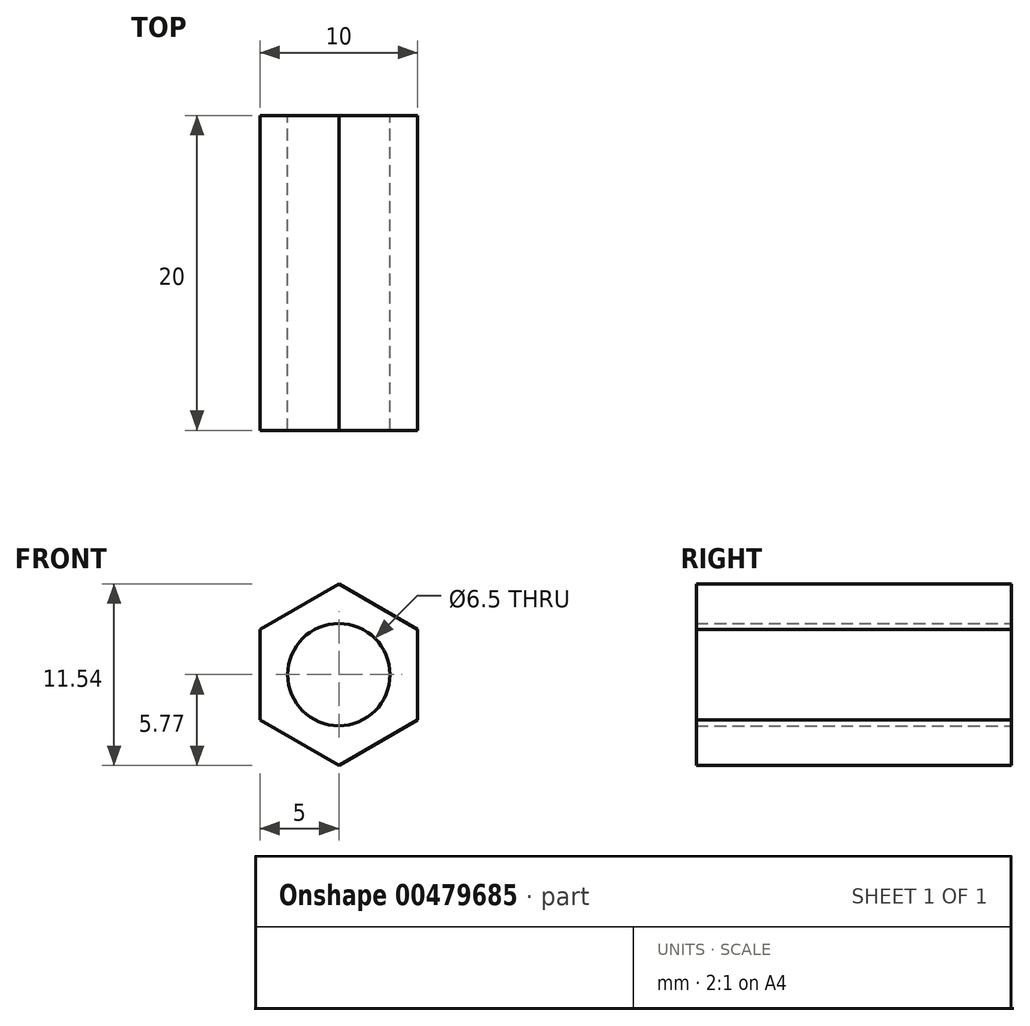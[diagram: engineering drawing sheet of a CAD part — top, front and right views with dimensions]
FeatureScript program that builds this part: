
annotation { "Feature Type Name" : "Feature", "Feature Type Description" : "" }
export const myFeature = defineFeature(function(context is Context, id is Id, definition is map)
    precondition{}
    {
        {
            var Q0;
            Q0=qCreatedBy(makeId("Front.planeOp"),FACE);
            var sketch = newSketch(context, id + "F0", { "sketchPlane" : qUnion([Q0])});
            skLineSegment(sketch, "E0.bottom", {"start": v(5, -5) * mm, "end": v(1.34, -5) * mm});
            skLineSegment(sketch, "E0.left", {"start": v(5, -2.89) * mm, "end": v(5, 2.89) * mm});
            skLineSegment(sketch, "E0.right", {"start": v(-5, -5) * mm, "end": v(-5, 5) * mm});
            skCircle(sketch, "E1", {"center": v(0, 0) * mm, "radius": 5 * mm});
            skPoint(sketch, "E2.start.orphan", {"position": v(5, 0) * mm});
            skPoint(sketch, "E3.orphan", {"position": v(-5, 0) * mm});
            skLineSegment(sketch, "E4", {"start": v(1.34, 5) * mm, "end": v(5, 5) * mm});
            skLineSegment(sketch, "E5", {"start": v(-5, 2.89) * mm, "end": v(-8.07, 4.66) * mm});
            skLineSegment(sketch, "E6", {"start": v(-5, -2.89) * mm, "end": v(-7.12, -4.11) * mm});
            skLineSegment(sketch, "E7", {"start": v(-7.12, -4.11) * mm, "end": v(-5, -2.89) * mm});
            skLineSegment(sketch, "E8", {"start": v(0, -8.43) * mm, "end": v(0, -5.77) * mm});
            skLineSegment(sketch, "E9", {"start": v(5, -2.89) * mm, "end": v(7.12, -4.11) * mm});
            skLineSegment(sketch, "E10", {"start": v(5, 2.89) * mm, "end": v(9.86, 5.7) * mm});
            skLineSegment(sketch, "E11", {"start": v(5, 2.89) * mm, "end": v(0, 5.77) * mm});
            skLineSegment(sketch, "E12", {"start": v(0, 5.77) * mm, "end": v(-5, 2.89) * mm});
            skLineSegment(sketch, "E13", {"start": v(-5, -2.89) * mm, "end": v(0, -5.77) * mm});
            skLineSegment(sketch, "E14", {"start": v(0, -5.77) * mm, "end": v(5, -2.89) * mm});
            skCircle(sketch, "E15", {"center": v(0, 0) * mm, "radius": 3.25 * mm});
            skLineSegment(sketch, "E16.trimOffspring", {"start": v(-1.34, 5) * mm, "end": v(-5, 5) * mm});
            skLineSegment(sketch, "E17.trimOffspring", {"start": v(-1.34, -5) * mm, "end": v(-5, -5) * mm});
            skPoint(sketch, "E18.orphan", {"position": v(0, 5) * mm});
            skSolve(sketch);
        }
        {
            var Q0;
            {var subQ1=sQuery(id+"F0.wireOp",EDGE,"E11");var subQ4=makeQuery(id+"F0.imprint","IMPRINT",VERTEX,{"derivedFrom":subQ1});Q0=makeQuery(id+"F0.imprint","IMPRINT",FACE,{"disambiguationData":[TD([[makeQuery(id+"F0.imprint","IMPRINT",EDGE,{"disambiguationData":[TD([[subQ4,1.0]])],"derivedFrom":subQ1}),1.0]])]});}
            var Q1;
            {var subQ0=sQuery(id+"F0.wireOp",EDGE,"E12");var subQ1=sQuery(id+"F0.wireOp",EDGE,"E0.right");var subQ2=makeQuery(id+"F0.imprint","INTERSECT",VERTEX,{"derivedFrom":[subQ1,subQ0]});Q1=makeQuery(id+"F0.imprint","IMPRINT",FACE,{"disambiguationData":[TD([[makeQuery(id+"F0.imprint","IMPRINT",EDGE,{"disambiguationData":[TD([[subQ2,1.0]])],"derivedFrom":subQ1}),-1.0]])]});}
            var Q2;
            {var subQ0=sQuery(id+"F0.wireOp",EDGE,"E13");var subQ1=sQuery(id+"F0.wireOp",EDGE,"E0.right");var subQ2=makeQuery(id+"F0.imprint","INTERSECT",VERTEX,{"derivedFrom":[subQ1,subQ0]});Q2=makeQuery(id+"F0.imprint","IMPRINT",FACE,{"disambiguationData":[TD([[makeQuery(id+"F0.imprint","IMPRINT",EDGE,{"disambiguationData":[TD([[subQ2,-1.0]])],"derivedFrom":subQ1}),-1.0]])]});}
            var Q3;
            {var subQ0=sQuery(id+"F0.wireOp",EDGE,"E14");var subQ1=makeQuery(id+"F0.imprint","IMPRINT",VERTEX,{"derivedFrom":subQ0});Q3=makeQuery(id+"F0.imprint","IMPRINT",FACE,{"disambiguationData":[TD([[makeQuery(id+"F0.imprint","IMPRINT",EDGE,{"disambiguationData":[TD([[subQ1,1.0]])],"derivedFrom":subQ0}),1.0]])]});}
            var Q4;
            {var subQ0=sQuery(id+"F0.wireOp",EDGE,"E14");var subQ1=sQuery(id+"F0.wireOp",EDGE,"E0.left");var subQ2=makeQuery(id+"F0.imprint","INTERSECT",VERTEX,{"derivedFrom":[subQ1,subQ0]});Q4=makeQuery(id+"F0.imprint","IMPRINT",FACE,{"disambiguationData":[TD([[makeQuery(id+"F0.imprint","IMPRINT",EDGE,{"disambiguationData":[TD([[subQ2,-1.0]])],"derivedFrom":subQ1}),1.0]])]});}
            var Q5;
            Q5=makeQuery(id+"F0.imprint","IMPRINT",FACE,{"disambiguationData":[TD([[makeQuery(id+"F0.imprint","IMPRINT",EDGE,{"derivedFrom":sQuery(id+"F0.wireOp",EDGE,"E15")}),-1.0]])]});
            var Q6;
            {var subQ0=sQuery(id+"F0.wireOp",EDGE,"E11");var subQ1=sQuery(id+"F0.wireOp",EDGE,"E0.left");var subQ2=makeQuery(id+"F0.imprint","INTERSECT",VERTEX,{"derivedFrom":[subQ1,subQ0]});Q6=makeQuery(id+"F0.imprint","IMPRINT",FACE,{"disambiguationData":[TD([[makeQuery(id+"F0.imprint","IMPRINT",EDGE,{"disambiguationData":[TD([[subQ2,1.0]])],"derivedFrom":subQ1}),1.0]])]});}
            extrude(context, id + "F1", {"entities" : qUnion([Q0, Q1, Q2, Q3, Q4, Q5, Q6]), "depth" : 20 * mm});
        }
    });
